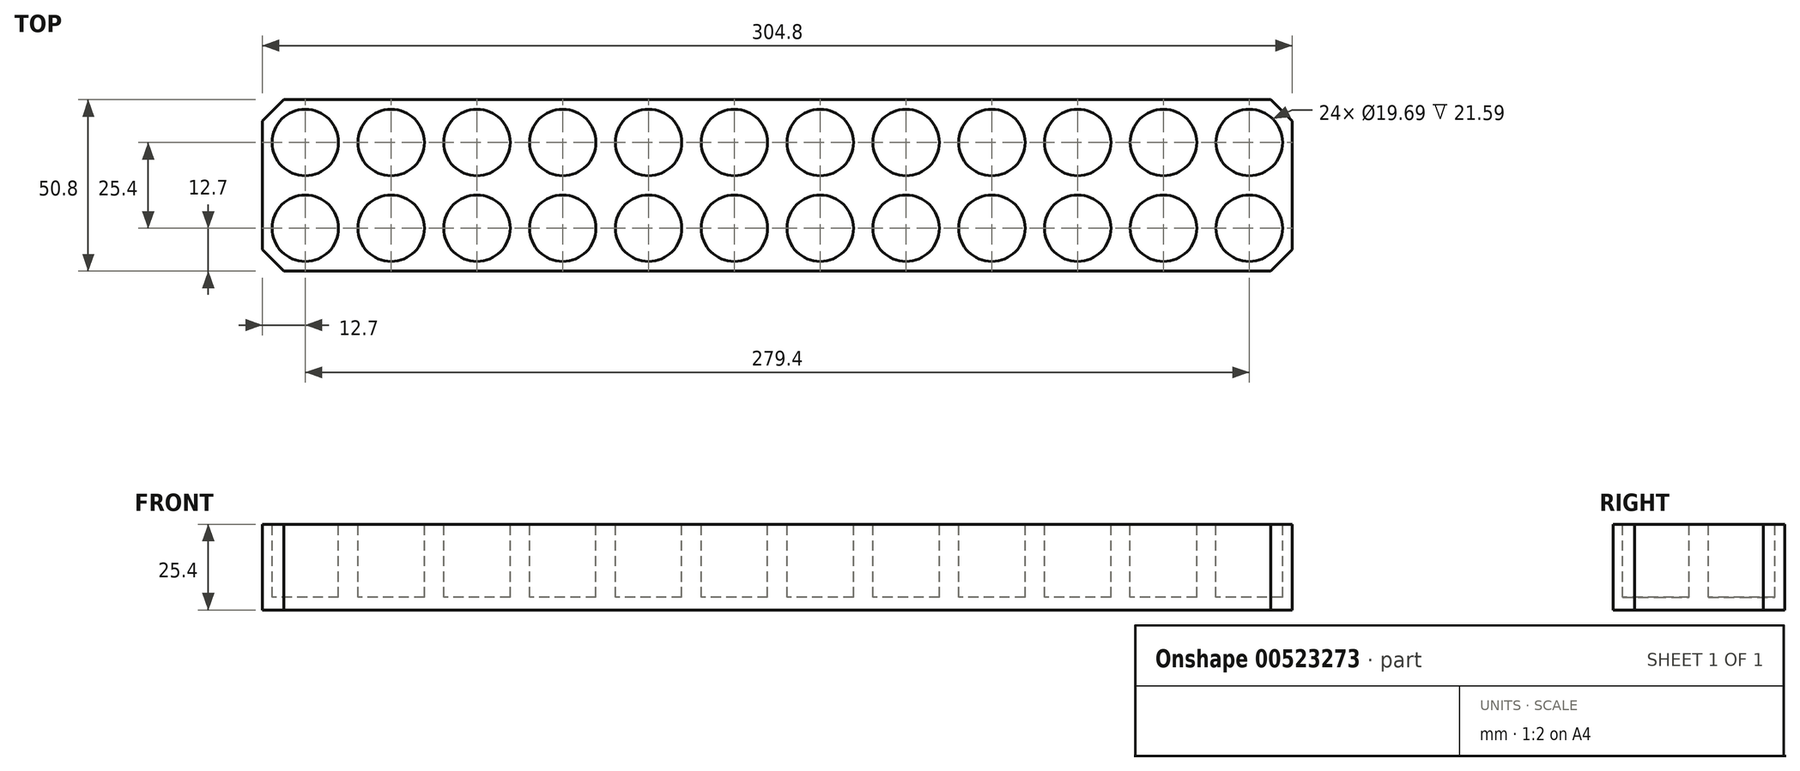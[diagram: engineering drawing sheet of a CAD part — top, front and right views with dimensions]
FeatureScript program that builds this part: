
annotation { "Feature Type Name" : "Feature", "Feature Type Description" : "" }
export const myFeature = defineFeature(function(context is Context, id is Id, definition is map)
    precondition{}
    {
        {
            var Q0;
            Q0=qCreatedBy(makeId("Top.planeOp"),FACE);
            var sketch = newSketch(context, id + "F0", { "sketchPlane" : qUnion([Q0])});
            skLineSegment(sketch, "E0.bottom", {"start": v(0, 0) * mm, "end": v(-304.8, 0) * mm});
            skLineSegment(sketch, "E0.top", {"start": v(0, -50.8) * mm, "end": v(-304.8, -50.8) * mm});
            skLineSegment(sketch, "E0.left", {"start": v(0, 0) * mm, "end": v(0, -50.8) * mm});
            skLineSegment(sketch, "E0.right", {"start": v(-304.8, 0) * mm, "end": v(-304.8, -50.8) * mm});
            skSolve(sketch);
        }
        {
            var Q0;
            Q0 = qSketchRegion(id + "F0", true);
            extrude(context, id + "F1", {"entities" : qUnion([Q0]), "oppositeDirection" : true, "depth" : 25.4 * mm, "offsetDistance" : 25.4 * mm});
        }
        {
            var Q0;
            Q0=makeQuery(id+"F1.opExtrude","SWEPT_EDGE",EDGE,{"disambiguationData":[OSD([sQuery(id+"F0.wireOp",EDGE,"E0.bottom"),sQuery(id+"F0.wireOp",EDGE,"E0.left")])]});
            var Q1;
            Q1=makeQuery(id+"F1.opExtrude","SWEPT_EDGE",EDGE,{"disambiguationData":[OSD([sQuery(id+"F0.wireOp",EDGE,"E0.top"),sQuery(id+"F0.wireOp",EDGE,"E0.left")])]});
            var Q2;
            Q2=makeQuery(id+"F1.opExtrude","SWEPT_EDGE",EDGE,{"disambiguationData":[OSD([sQuery(id+"F0.wireOp",EDGE,"E0.top"),sQuery(id+"F0.wireOp",EDGE,"E0.right")])]});
            var Q3;
            Q3=makeQuery(id+"F1.opExtrude","SWEPT_EDGE",EDGE,{"disambiguationData":[OSD([sQuery(id+"F0.wireOp",EDGE,"E0.bottom"),sQuery(id+"F0.wireOp",EDGE,"E0.right")])]});
            chamfer(context, id + "F2", {"entities" : qUnion([Q0, Q1, Q2, Q3]), "width" : 6.35 * mm, "tangentPropagation" : true});
        }
        {
            var Q0;
            Q0=makeQuery(id+"F1.opExtrude","CAP_FACE",FACE,{"disambiguationData":[OSD([sQuery(id+"F0.wireOp",EDGE,"E0.bottom"),sQuery(id+"F0.wireOp",EDGE,"E0.top"),sQuery(id+"F0.wireOp",EDGE,"E0.left"),sQuery(id+"F0.wireOp",EDGE,"E0.right")])],"isStart":true});
            var sketch = newSketch(context, id + "F3", { "sketchPlane" : qUnion([Q0])});
            skCircle(sketch, "E1", {"center": v(-12.7, -12.7) * mm, "radius": 9.84 * mm});
            skCircle(sketch, "E2.0.1.0", {"center": v(-12.7, -38.1) * mm, "radius": 9.84 * mm});
            skCircle(sketch, "E2.1.0.0", {"center": v(-38.1, -12.7) * mm, "radius": 9.84 * mm});
            skCircle(sketch, "E2.1.1.0", {"center": v(-38.1, -38.1) * mm, "radius": 9.84 * mm});
            skCircle(sketch, "E2.2.0.0", {"center": v(-63.5, -12.7) * mm, "radius": 9.84 * mm});
            skCircle(sketch, "E2.2.1.0", {"center": v(-63.5, -38.1) * mm, "radius": 9.84 * mm});
            skCircle(sketch, "E2.3.0.0", {"center": v(-88.9, -12.7) * mm, "radius": 9.84 * mm});
            skCircle(sketch, "E2.3.1.0", {"center": v(-88.9, -38.1) * mm, "radius": 9.84 * mm});
            skCircle(sketch, "E2.4.0.0", {"center": v(-114.3, -12.7) * mm, "radius": 9.84 * mm});
            skCircle(sketch, "E2.4.1.0", {"center": v(-114.3, -38.1) * mm, "radius": 9.84 * mm});
            skCircle(sketch, "E2.5.0.0", {"center": v(-139.7, -12.7) * mm, "radius": 9.84 * mm});
            skCircle(sketch, "E2.5.1.0", {"center": v(-139.7, -38.1) * mm, "radius": 9.84 * mm});
            skCircle(sketch, "E2.6.0.0", {"center": v(-165.1, -12.7) * mm, "radius": 9.84 * mm});
            skCircle(sketch, "E2.6.1.0", {"center": v(-165.1, -38.1) * mm, "radius": 9.84 * mm});
            skCircle(sketch, "E2.7.0.0", {"center": v(-190.5, -12.7) * mm, "radius": 9.84 * mm});
            skCircle(sketch, "E2.7.1.0", {"center": v(-190.5, -38.1) * mm, "radius": 9.84 * mm});
            skCircle(sketch, "E2.8.0.0", {"center": v(-215.9, -12.7) * mm, "radius": 9.84 * mm});
            skCircle(sketch, "E2.8.1.0", {"center": v(-215.9, -38.1) * mm, "radius": 9.84 * mm});
            skCircle(sketch, "E2.9.0.0", {"center": v(-241.3, -12.7) * mm, "radius": 9.84 * mm});
            skCircle(sketch, "E2.9.1.0", {"center": v(-241.3, -38.1) * mm, "radius": 9.84 * mm});
            skCircle(sketch, "E2.10.0.0", {"center": v(-266.7, -12.7) * mm, "radius": 9.84 * mm});
            skCircle(sketch, "E2.10.1.0", {"center": v(-266.7, -38.1) * mm, "radius": 9.84 * mm});
            skCircle(sketch, "E2.11.0.0", {"center": v(-292.1, -12.7) * mm, "radius": 9.84 * mm});
            skCircle(sketch, "E2.11.1.0", {"center": v(-292.1, -38.1) * mm, "radius": 9.84 * mm});
            skLineSegment(sketch, "E2.direction1", {"start": v(-12.7, -12.7) * mm, "end": v(-38.1, -12.7) * mm, "construction": true});
            skLineSegment(sketch, "E2.direction2", {"start": v(-12.7, -12.7) * mm, "end": v(-12.7, -38.1) * mm, "construction": true});
            skSolve(sketch);
        }
        {
            var Q0;
            Q0 = qSketchRegion(id + "F3", true);
            extrude(context, id + "F4", {"entities" : qUnion([Q0]), "operationType" : NewBodyOperationType.REMOVE, "oppositeDirection" : true, "depth" : 21.59 * mm, "offsetDistance" : 25.4 * mm});
        }
    });
